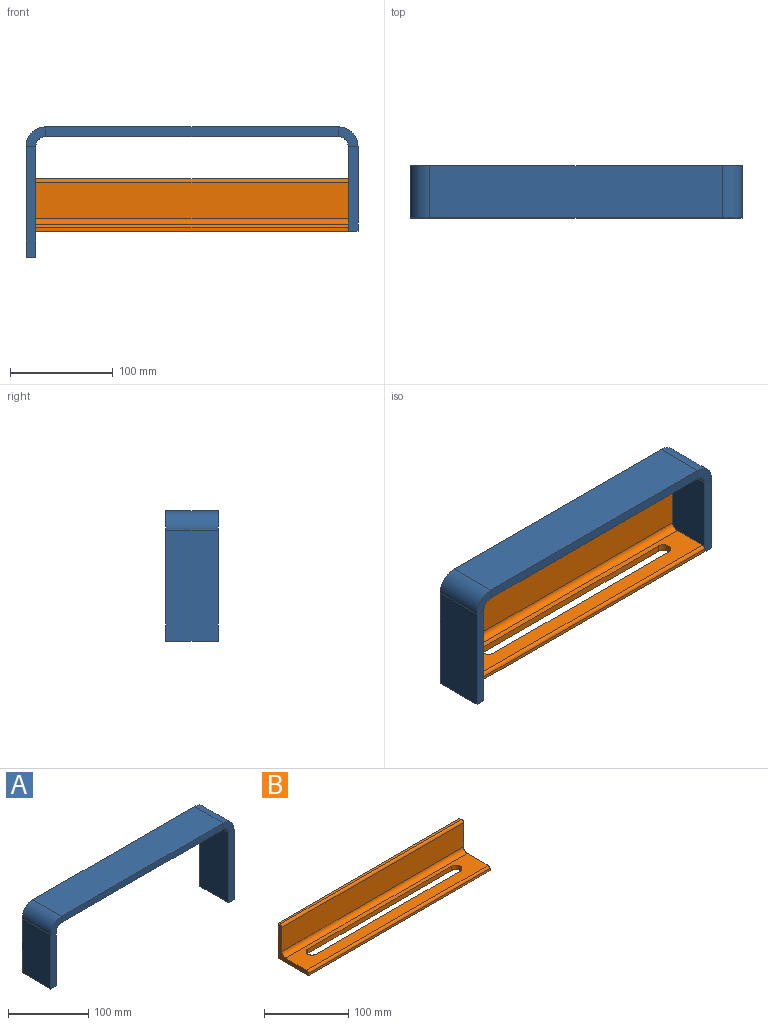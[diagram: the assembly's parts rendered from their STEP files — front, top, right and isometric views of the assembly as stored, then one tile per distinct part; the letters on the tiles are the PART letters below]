
ASSEMBLY  parts=2 mates=1
PART A: 22 faces, bbox 323.9x50.8x127 mm
  f0: plane 285.75x9.53mm, normal (0,1,0), area 2721.8mm2, adj f2,f3,f10,f19
  f1: plane 285.75x9.53mm, normal (0,-1,0), area 2721.8mm2, adj f2,f3,f9,f18
  f2: plane 285.75x50.8mm, normal (0,0,1), area 14516.1mm2, adj f0,f1,f11,f20
  f3: plane 285.75x50.8mm, normal (0,0,-1), area 14516.1mm2, adj f0,f1,f12,f21
  f4: plane 50.8x9.53mm, normal (0,0,-1), area 483.9mm2, adj f5,f6,f7,f8
  f5: plane 107.95x9.53mm, normal (0,1,0), area 1028.2mm2, adj f4,f7,f8,f10
  f6: plane 107.95x9.53mm, normal (0,-1,0), area 1028.2mm2, adj f4,f7,f8,f9
  f7: plane 107.95x50.8mm, normal (1,0,0), area 5483.9mm2, adj f4,f5,f6,f11
  f8: plane 107.95x50.8mm, normal (-1,0,0), area 5483.9mm2, adj f4,f5,f6,f12
  f9: plane 19.05x19.05mm, normal (0,-1,0), area 213.8mm2, adj f1,f6,f11,f12
  f10: plane 19.05x19.05mm, normal (0,1,0), area 213.8mm2, adj f0,f5,f11,f12
  f11: cylinder r=19.05mm len=50.8mm, axis (0,-1,0), area 1520.1mm2, adj f2,f7,f9,f10
  f12: cylinder r=9.53mm len=50.8mm, axis (0,-1,0), area 760.1mm2, adj f3,f8,f9,f10
  f13: plane 50.8x9.53mm, normal (0,0,-1), area 483.9mm2, adj f14,f15,f16,f17
  f14: plane 82.55x9.53mm, normal (0,-1,0), area 786.3mm2, adj f13,f16,f17,f18
  f15: plane 82.55x9.53mm, normal (0,1,0), area 786.3mm2, adj f13,f16,f17,f19
  f16: plane 82.55x50.8mm, normal (-1,0,0), area 4193.5mm2, adj f13,f14,f15,f20
  f17: plane 82.55x50.8mm, normal (1,0,0), area 4193.5mm2, adj f13,f14,f15,f21
  f18: plane 19.05x19.05mm, normal (0,-1,0), area 213.8mm2, adj f1,f14,f20,f21
  f19: plane 19.05x19.05mm, normal (0,1,0), area 213.8mm2, adj f0,f15,f20,f21
  f20: cylinder r=19.05mm len=50.8mm, axis (0,-1,0), area 1520.1mm2, adj f2,f16,f18,f19
  f21: cylinder r=9.53mm len=50.8mm, axis (0,-1,0), area 760.1mm2, adj f3,f17,f18,f19
PART B: 15 faces, bbox 304.8x50.8x50.8 mm
  f0: plane 50.8x50.8mm, normal (1,0,0), area 609.2mm2, adj f2,f3,f4,f5,f6,f7,f8,f9
  f1: plane 50.8x50.8mm, normal (-1,0,0), area 609.2mm2, adj f2,f3,f4,f5,f6,f7,f8,f9
  f2: cylinder r=3.17mm len=304.8mm, axis (-1,0,0), area 1520.1mm2, adj f0,f1,f3,f10
  f3: plane 304.8x34.93mm, normal (0,0,1), area 7037.2mm2, adj f0,f1,f2,f4,f11,f12,f13,f14
  f4: cylinder r=6.35mm len=304.8mm, axis (-1,0,0), area 3040.3mm2, adj f0,f1,f3,f5
  f5: plane 304.8x34.93mm, normal (0,-1,0), area 10645.1mm2, adj f0,f1,f4,f6
  f6: cylinder r=3.17mm len=304.8mm, axis (-1,0,0), area 1520.1mm2, adj f0,f1,f5,f7
  f7: plane 304.8x3.18mm, normal (0,0,1), area 967.7mm2, adj f0,f1,f6,f8
  f8: plane 304.8x50.8mm, normal (0,1,0), area 15483.8mm2, adj f0,f1,f7,f9
  f9: plane 304.8x50.8mm, normal (0,0,-1), area 11875.9mm2, adj f0,f1,f8,f10,f11,f12,f13,f14
  f10: plane 304.8x3.18mm, normal (0,-1,0), area 967.7mm2, adj f0,f1,f2,f9
  f11: plane 241.3x6.35mm, normal (0,1,0), area 1532.3mm2, adj f3,f9,f12,f14
  f12: cylinder r=7.14mm len=14.29mm, axis (0,0,-1), area 142.5mm2, adj f3,f9,f11,f13
  f13: plane 241.3x6.35mm, normal (0,-1,0), area 1532.3mm2, adj f3,f9,f12,f14
  f14: cylinder r=7.14mm len=14.29mm, axis (0,0,-1), area 142.5mm2, adj f3,f9,f11,f13
PLACE A rot(axis=(0,0,1),180deg) t=(-273.1,-117.54,33)mm
PLACE B t=(31.7,-66.74,-59.07)mm
MATE fastened A.f17 <-> B.f0  axis (-1,0,0) through (31.7,-117.54,-59.07)mm
